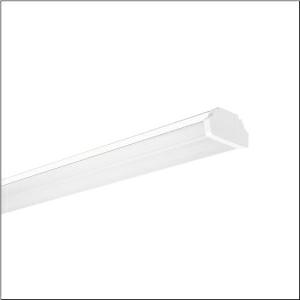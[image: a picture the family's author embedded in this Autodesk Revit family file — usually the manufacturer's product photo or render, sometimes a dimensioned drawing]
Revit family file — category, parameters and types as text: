
# Revit family: dus_r__31_ho_53bd812d2v6120_f11a
name_source: partatom
category: Lighting Fixtures
units: mm (PartAtom-declared; Revit-internal decimal feet)

## family parameters
Cut with Voids When Loaded = No
Host = Face
Light Source = No
Part Type = Normal
Room Calculation Point = No
Round Connector Dimension = Use Diameter
Shared = No

## types (1)
- --- (1 x LED, 12400 lm, 79.5 W, 6500K)
    Apparent Load = 80 VA
    CIE Flux Codes = 47 80 95 92 100
    Color Rendering = 80
    Color Temperature = 6500K
    Default Elevation = 1800 mm
    Description = DUS® 31 HO, luminaire insert, of sheet steel, coil coated, white, length: 1.535mm, width: 81mm, height: 90mm, 5x system unit, system units: 307mm, LED rated luminous flux: 12.400lm, light colour: 865, control gear: DALI 2, control gear: ECG DALI, with plug, 5-pole, with phase selection, mains connection: 220..240V, AC, 50/60Hz, rated input power: 80W, through-wiring accessed according to module size, primary optical cover: cover, of PMMA, light emission: direct distribution, primary light characteristic: symmetric, protection rating (complete): IP20, protection rating (LED compartment): IP50, insulation class (complete): insulation class I (protective earthing), certification: CE, ENEC, VDE, UKCA, impact resistance: IK03, permissible ambient temperature for indoor applications: -25..+30°C, corresponds to IFS (International Featured Standards) requirements for safety and quality in the food industry, reducing of maximum allowable ambient temperature of 5°C with ceiling mounting, packaging unit: 1 piece
    Height = 95 mm
    Lamp = 1 x LED
    Lamp Light Flux = 12400 lm
    Lamp Power = 79.5 W
    Lamp count = 1
    Length = 1535 mm
    Luminous efficacy = 156 lm/W
    Manufacturer = Siteco
    ModVariant = No
    Model = 53BD812D2V6120
    Mounting Place = Ceiling
    Mounting Type = Pendant
    Number of Poles = 1
    OnlyDefault = Yes
    Power Factor = 1
    Product Name = DUS® 31 HO
    Product group = luminaire insert
    ProductGroupID = 901
    Protection Class = Protection class I
    Protection Degree = IP 20
    RLX_Detail_Level = 1
    RLX_Emergency_Light_Flux = 0 lm
    RLX_Emergency_Type = 0
    RLX_Emergency_Type_DB = No
    RlxData = <blob elided: 42193 chars, md5=026a0602>
    Socket = socket
    Standby Power = 0 W
    System Light Flux = 12400 lm
    System Power = 80 W
    Type Comments = factory setting: luminous flux: 100 % | dim-lin: 254 | 345 mA
    Type Image = l_1313537.jpg
    URL = http://relux.com
    VarID = @adj_156031
    Voltage = 0 V
    Weight = 0.00 kg
    Width = 81 mm

## geometry (parser evidence)
native form markers: Blend x4, Sweep x13
no freeform markers — native parametric forms only
